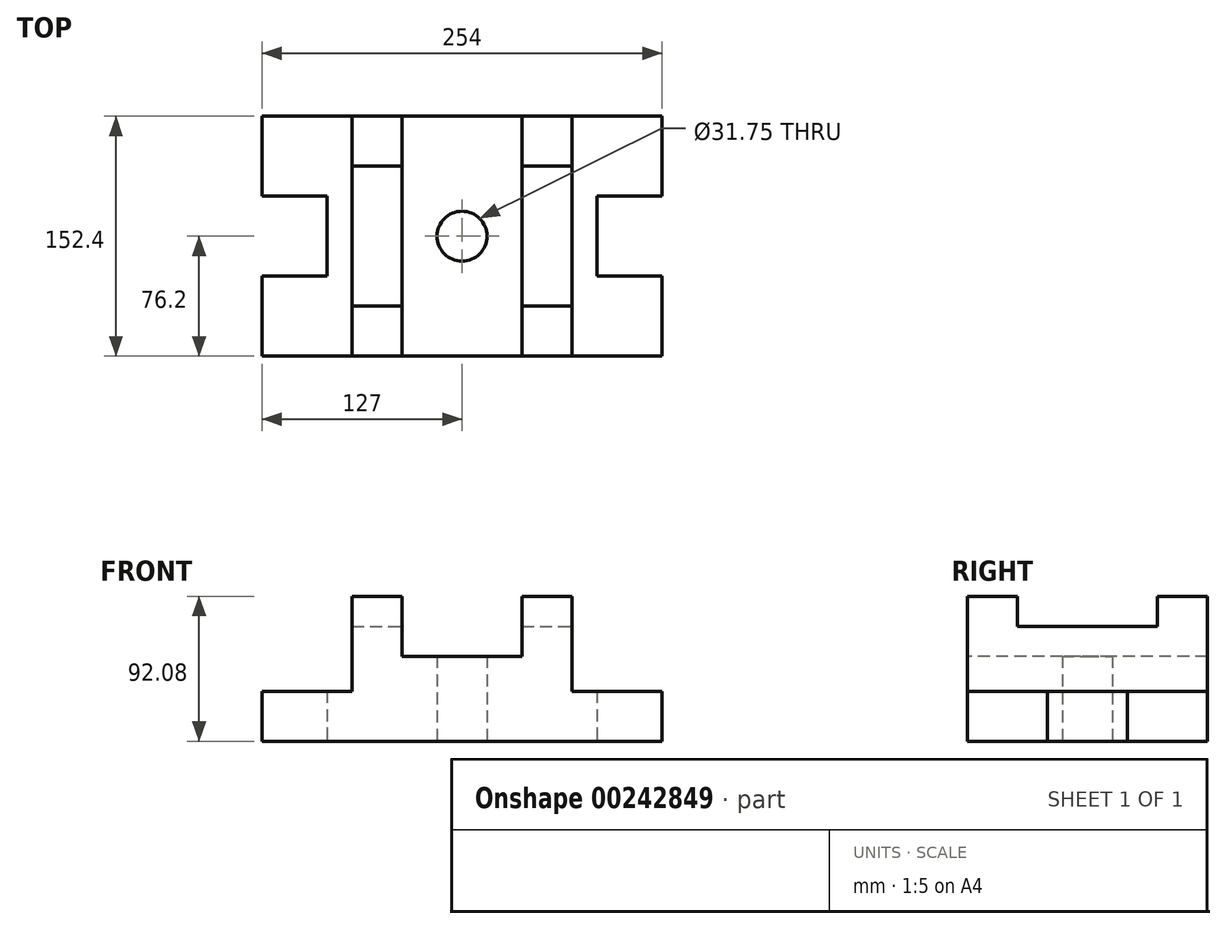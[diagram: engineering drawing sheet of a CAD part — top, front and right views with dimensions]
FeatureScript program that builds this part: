
annotation { "Feature Type Name" : "Feature", "Feature Type Description" : "" }
export const myFeature = defineFeature(function(context is Context, id is Id, definition is map)
    precondition{}
    {
        {
            var Q0;
            Q0=qCreatedBy(makeId("Top.planeOp"),FACE);
            var sketch = newSketch(context, id + "F0", { "sketchPlane" : qUnion([Q0])});
            skCircle(sketch, "E0", {"center": v(0, 0) * mm, "radius": 15.88 * mm});
            skLineSegment(sketch, "E1.bottom", {"start": v(-127, 76.2) * mm, "end": v(127, 76.2) * mm});
            skLineSegment(sketch, "E1.top", {"start": v(-127, -76.2) * mm, "end": v(127, -76.2) * mm});
            skLineSegment(sketch, "E1.left", {"start": v(-127, 76.2) * mm, "end": v(-127, -76.2) * mm});
            skLineSegment(sketch, "E1.right", {"start": v(127, 76.2) * mm, "end": v(127, -76.2) * mm});
            skLineSegment(sketch, "E2.bottom", {"start": v(127, 25.4) * mm, "end": v(85.72, 25.4) * mm});
            skLineSegment(sketch, "E2.top", {"start": v(127, -25.4) * mm, "end": v(85.72, -25.4) * mm});
            skLineSegment(sketch, "E2.right", {"start": v(85.72, 25.4) * mm, "end": v(85.72, -25.4) * mm});
            skLineSegment(sketch, "E3.bottom", {"start": v(-127, 25.4) * mm, "end": v(-85.72, 25.4) * mm});
            skLineSegment(sketch, "E3.top", {"start": v(-127, -25.4) * mm, "end": v(-85.72, -25.4) * mm});
            skLineSegment(sketch, "E3.right", {"start": v(-85.72, 25.4) * mm, "end": v(-85.72, -25.4) * mm});
            skSolve(sketch);
        }
        {
            var Q0;
            Q0=makeQuery(id+"F0.imprint","IMPRINT",FACE,{"disambiguationData":[TD([[makeQuery(id+"F0.imprint","IMPRINT",EDGE,{"derivedFrom":sQuery(id+"F0.wireOp",EDGE,"E0")}),-1.0]])]});
            extrude(context, id + "F1", {"entities" : qUnion([Q0]), "depth" : 31.75 * mm});
        }
        {
            var Q0;
            Q0=makeQuery(id+"F1.opExtrude","CAP_FACE",FACE,{"disambiguationData":[OSD([sQuery(id+"F0.wireOp",EDGE,"E0"),sQuery(id+"F0.wireOp",EDGE,"E1.bottom"),sQuery(id+"F0.wireOp",EDGE,"E1.top"),sQuery(id+"F0.wireOp",EDGE,"E1.left"),sQuery(id+"F0.wireOp",EDGE,"E1.right"),sQuery(id+"F0.wireOp",EDGE,"E2.bottom"),sQuery(id+"F0.wireOp",EDGE,"E2.top"),sQuery(id+"F0.wireOp",EDGE,"E2.right"),sQuery(id+"F0.wireOp",EDGE,"E3.bottom"),sQuery(id+"F0.wireOp",EDGE,"E3.top"),sQuery(id+"F0.wireOp",EDGE,"E3.right")])],"isStart":false});
            var sketch = newSketch(context, id + "F2", { "sketchPlane" : qUnion([Q0])});
            skCircle(sketch, "E4", {"center": v(0, 0) * mm, "radius": 15.88 * mm});
            skLineSegment(sketch, "E5.bottom", {"start": v(-69.85, 76.2) * mm, "end": v(69.85, 76.2) * mm});
            skLineSegment(sketch, "E5.top", {"start": v(-69.85, -76.2) * mm, "end": v(69.85, -76.2) * mm});
            skLineSegment(sketch, "E5.left", {"start": v(-69.85, 76.2) * mm, "end": v(-69.85, -76.2) * mm});
            skLineSegment(sketch, "E5.right", {"start": v(69.85, 76.2) * mm, "end": v(69.85, -76.2) * mm});
            skSolve(sketch);
        }
        {
            var Q0;
            Q0 = qSketchRegion(id + "F2", true);
            extrude(context, id + "F3", {"entities" : qUnion([Q0]), "operationType" : NewBodyOperationType.ADD, "depth" : 22.22 * mm});
        }
        {
            var Q0;
            Q0=makeQuery(id+"F3.opExtrude","CAP_FACE",FACE,{"disambiguationData":[OSD([sQuery(id+"F2.wireOp",EDGE,"E4"),sQuery(id+"F2.wireOp",EDGE,"E5.bottom"),sQuery(id+"F2.wireOp",EDGE,"E5.top"),sQuery(id+"F2.wireOp",EDGE,"E5.left"),sQuery(id+"F2.wireOp",EDGE,"E5.right")])],"isStart":false});
            var sketch = newSketch(context, id + "F4", { "sketchPlane" : qUnion([Q0])});
            skLineSegment(sketch, "E6.bottom", {"start": v(-69.85, 76.2) * mm, "end": v(-38.1, 76.2) * mm});
            skLineSegment(sketch, "E6.top", {"start": v(-69.85, -76.2) * mm, "end": v(-38.1, -76.2) * mm});
            skLineSegment(sketch, "E6.left", {"start": v(-69.85, 76.2) * mm, "end": v(-69.85, -76.2) * mm});
            skLineSegment(sketch, "E6.right", {"start": v(-38.1, 76.2) * mm, "end": v(-38.1, -76.2) * mm});
            skLineSegment(sketch, "E7.bottom", {"start": v(69.85, 76.2) * mm, "end": v(38.1, 76.2) * mm});
            skLineSegment(sketch, "E7.top", {"start": v(69.85, -76.2) * mm, "end": v(38.1, -76.2) * mm});
            skLineSegment(sketch, "E7.left", {"start": v(69.85, 76.2) * mm, "end": v(69.85, -76.2) * mm});
            skLineSegment(sketch, "E7.right", {"start": v(38.1, 76.2) * mm, "end": v(38.1, -76.2) * mm});
            skSolve(sketch);
        }
        {
            var Q0;
            Q0 = qSketchRegion(id + "F4", true);
            extrude(context, id + "F5", {"entities" : qUnion([Q0]), "operationType" : NewBodyOperationType.ADD, "depth" : 19.05 * mm});
        }
        {
            var Q0;
            Q0=makeQuery(id+"F5.opExtrude","CAP_FACE",FACE,{"disambiguationData":[OSD([sQuery(id+"F4.wireOp",EDGE,"E6.bottom"),sQuery(id+"F4.wireOp",EDGE,"E6.top"),sQuery(id+"F4.wireOp",EDGE,"E6.left"),sQuery(id+"F4.wireOp",EDGE,"E6.right")])],"isStart":false});
            var sketch = newSketch(context, id + "F6", { "sketchPlane" : qUnion([Q0])});
            skLineSegment(sketch, "E8.bottom", {"start": v(-69.85, 76.2) * mm, "end": v(-38.1, 76.2) * mm});
            skLineSegment(sketch, "E8.top", {"start": v(-69.85, 44.45) * mm, "end": v(-38.1, 44.45) * mm});
            skLineSegment(sketch, "E8.left", {"start": v(-69.85, 76.2) * mm, "end": v(-69.85, 44.45) * mm});
            skLineSegment(sketch, "E8.right", {"start": v(-38.1, 76.2) * mm, "end": v(-38.1, 44.45) * mm});
            skLineSegment(sketch, "E9.bottom", {"start": v(-69.85, -44.45) * mm, "end": v(-38.1, -44.45) * mm});
            skLineSegment(sketch, "E9.top", {"start": v(-69.85, -76.2) * mm, "end": v(-38.1, -76.2) * mm});
            skLineSegment(sketch, "E9.left", {"start": v(-69.85, -44.45) * mm, "end": v(-69.85, -76.2) * mm});
            skLineSegment(sketch, "E9.right", {"start": v(-38.1, -44.45) * mm, "end": v(-38.1, -76.2) * mm});
            skSolve(sketch);
        }
        {
            var Q0;
            Q0 = qSketchRegion(id + "F6", true);
            extrude(context, id + "F7", {"entities" : qUnion([Q0]), "operationType" : NewBodyOperationType.ADD, "depth" : 19.05 * mm});
        }
        {
            var Q0;
            Q0=makeQuery(id+"F5.opExtrude","CAP_FACE",FACE,{"disambiguationData":[OSD([sQuery(id+"F4.wireOp",EDGE,"E7.bottom"),sQuery(id+"F4.wireOp",EDGE,"E7.top"),sQuery(id+"F4.wireOp",EDGE,"E7.left"),sQuery(id+"F4.wireOp",EDGE,"E7.right")])],"isStart":false});
            var sketch = newSketch(context, id + "F8", { "sketchPlane" : qUnion([Q0])});
            skLineSegment(sketch, "E10.bottom", {"start": v(38.1, 76.2) * mm, "end": v(69.85, 76.2) * mm});
            skLineSegment(sketch, "E10.top", {"start": v(38.1, 44.45) * mm, "end": v(69.85, 44.45) * mm});
            skLineSegment(sketch, "E10.left", {"start": v(38.1, 76.2) * mm, "end": v(38.1, 44.45) * mm});
            skLineSegment(sketch, "E10.right", {"start": v(69.85, 76.2) * mm, "end": v(69.85, 44.45) * mm});
            skLineSegment(sketch, "E11.bottom", {"start": v(38.1, -76.2) * mm, "end": v(69.85, -76.2) * mm});
            skLineSegment(sketch, "E11.top", {"start": v(38.1, -44.45) * mm, "end": v(69.85, -44.45) * mm});
            skLineSegment(sketch, "E11.left", {"start": v(38.1, -76.2) * mm, "end": v(38.1, -44.45) * mm});
            skLineSegment(sketch, "E11.right", {"start": v(69.85, -76.2) * mm, "end": v(69.85, -44.45) * mm});
            skSolve(sketch);
        }
        {
            var Q0;
            Q0 = qSketchRegion(id + "F8", true);
            extrude(context, id + "F9", {"entities" : qUnion([Q0]), "operationType" : NewBodyOperationType.ADD, "depth" : 19.05 * mm});
        }
    });
